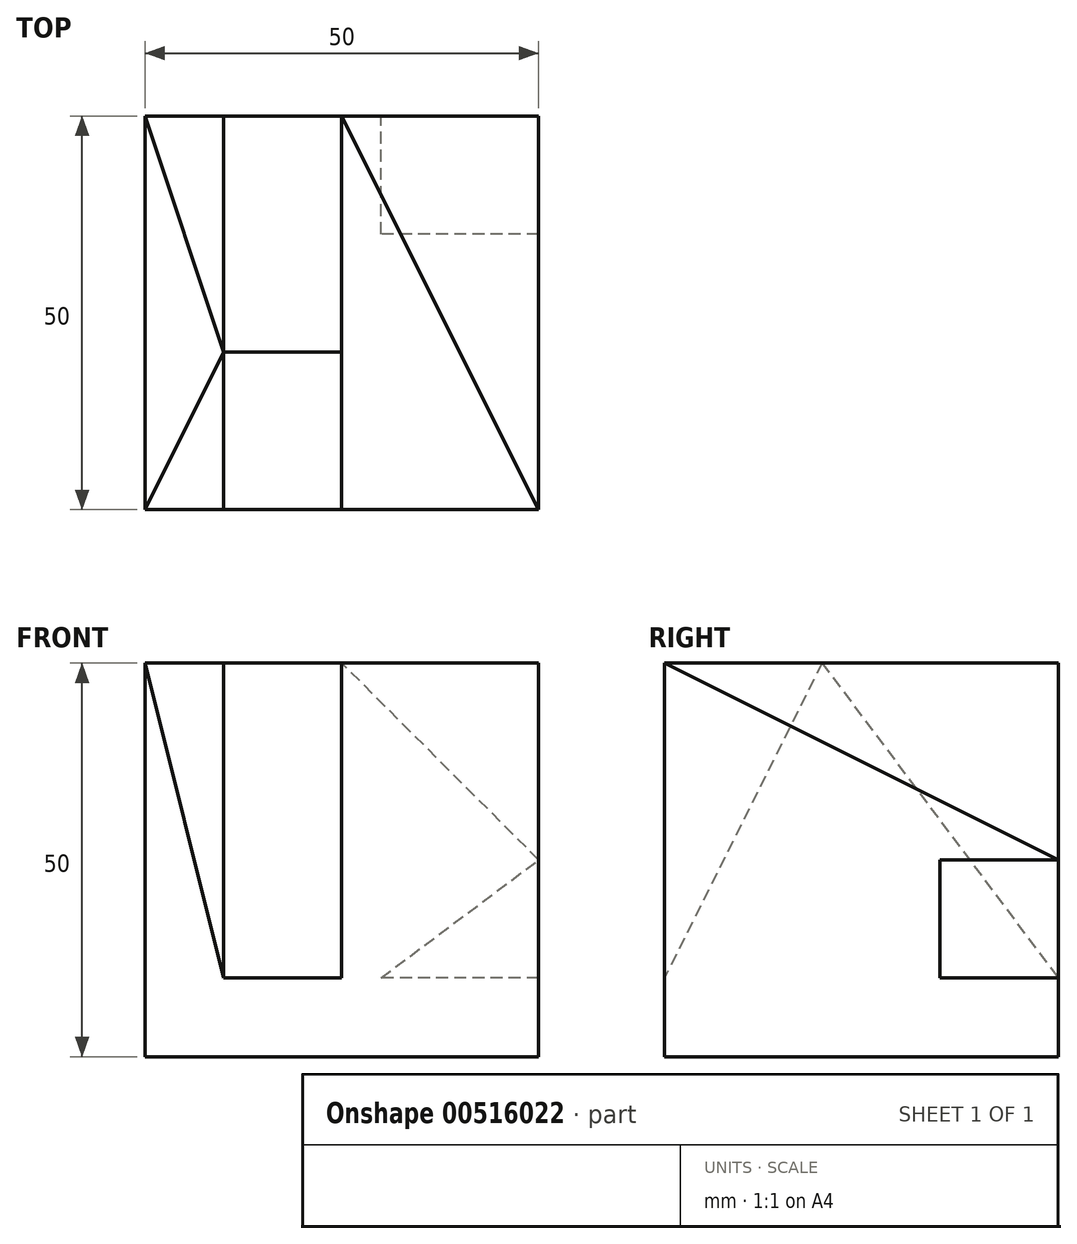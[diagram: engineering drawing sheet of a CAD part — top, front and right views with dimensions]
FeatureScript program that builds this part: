
annotation { "Feature Type Name" : "Feature", "Feature Type Description" : "" }
export const myFeature = defineFeature(function(context is Context, id is Id, definition is map)
    precondition{}
    {
        {
            var Q0;
            Q0=qCreatedBy(makeId("Top.planeOp"),FACE);
            var sketch = newSketch(context, id + "F0", { "sketchPlane" : qUnion([Q0])});
            skLineSegment(sketch, "E0.bottom", {"start": v(0, 0) * mm, "end": v(50, 0) * mm});
            skLineSegment(sketch, "E0.top", {"start": v(0, 50) * mm, "end": v(50, 50) * mm});
            skLineSegment(sketch, "E0.left", {"start": v(0, 0) * mm, "end": v(0, 50) * mm});
            skLineSegment(sketch, "E0.right", {"start": v(50, 0) * mm, "end": v(50, 50) * mm});
            skSolve(sketch);
        }
        {
            var Q0;
            Q0=makeQuery(id+"F0.imprint","IMPRINT",FACE,{"disambiguationData":[TD([[makeQuery(id+"F0.imprint","IMPRINT",EDGE,{"derivedFrom":sQuery(id+"F0.wireOp",EDGE,"E0.bottom")}),1.0]])]});
            extrude(context, id + "F1", {"entities" : qUnion([Q0]), "depth" : 50 * mm, "offsetDistance" : 25 * mm});
        }
        {
            var Q0;
            Q0=makeQuery(id+"F1.opExtrude","SWEPT_FACE",FACE,{"disambiguationData":[OSD([sQuery(id+"F0.wireOp",EDGE,"E0.top")])]});
            var sketch = newSketch(context, id + "F2", { "sketchPlane" : qUnion([Q0])});
            skLineSegment(sketch, "E1", {"start": v(-50, 10) * mm, "end": v(-30, 10) * mm});
            skLineSegment(sketch, "E2", {"start": v(-30, 10) * mm, "end": v(-50, 25) * mm});
            skLineSegment(sketch, "E3", {"start": v(-50, 25) * mm, "end": v(-50, 10) * mm});
            skSolve(sketch);
        }
        {
            var Q0;
            Q0=makeQuery(id+"F2.imprint","IMPRINT",FACE,{"disambiguationData":[TD([[makeQuery(id+"F2.imprint","IMPRINT",EDGE,{"derivedFrom":sQuery(id+"F2.wireOp",EDGE,"E1")}),1.0]])]});
            extrude(context, id + "F3", {"entities" : qUnion([Q0]), "operationType" : NewBodyOperationType.REMOVE, "oppositeDirection" : true, "depth" : 15 * mm, "offsetDistance" : 25 * mm});
        }
        {
            var Q0;
            Q0=makeQuery(id+"F1.opExtrude","CAP_FACE",FACE,{"disambiguationData":[OSD([sQuery(id+"F0.wireOp",EDGE,"E0.bottom"),sQuery(id+"F0.wireOp",EDGE,"E0.top"),sQuery(id+"F0.wireOp",EDGE,"E0.left"),sQuery(id+"F0.wireOp",EDGE,"E0.right")])],"isStart":false});
            var sketch = newSketch(context, id + "F4", { "sketchPlane" : qUnion([Q0])});
            skLineSegment(sketch, "E4.bottom", {"start": v(10, 0) * mm, "end": v(25, 0) * mm});
            skLineSegment(sketch, "E4.top", {"start": v(10, 20) * mm, "end": v(25, 20) * mm});
            skLineSegment(sketch, "E4.left", {"start": v(10, 0) * mm, "end": v(10, 20) * mm});
            skLineSegment(sketch, "E4.right", {"start": v(25, 0) * mm, "end": v(25, 20) * mm});
            skSolve(sketch);
        }
        {
            var Q0;
            Q0=makeQuery(id+"F1.opExtrude","SWEPT_FACE",FACE,{"disambiguationData":[OSD([sQuery(id+"F0.wireOp",EDGE,"E0.left")])]});
            var sketch = newSketch(context, id + "F5", { "sketchPlane" : qUnion([Q0])});
            skLineSegment(sketch, "E5", {"start": v(-20, 50) * mm, "end": v(0, 10) * mm});
            skSolve(sketch);
        }
        {
            var Q0;
            Q0=makeQuery(id+"F4.imprint","IMPRINT",FACE,{"disambiguationData":[TD([[makeQuery(id+"F4.imprint","IMPRINT",EDGE,{"derivedFrom":sQuery(id+"F4.wireOp",EDGE,"E4.bottom")}),1.0]])]});
            var Q1;
            Q1=sQuery(id+"F5.wireOp",EDGE,"E5");
            sweep(context, id + "F6", {"operationType" : NewBodyOperationType.REMOVE, "profiles" : qUnion([Q0]), "path" : qUnion([Q1])});
        }
        {
            var Q0;
            Q0=makeQuery(id+"F1.opExtrude","CAP_FACE",FACE,{"disambiguationData":[OSD([sQuery(id+"F0.wireOp",EDGE,"E0.bottom"),sQuery(id+"F0.wireOp",EDGE,"E0.top"),sQuery(id+"F0.wireOp",EDGE,"E0.left"),sQuery(id+"F0.wireOp",EDGE,"E0.right")])],"isStart":false});
            var sketch = newSketch(context, id + "F7", { "sketchPlane" : qUnion([Q0])});
            skLineSegment(sketch, "E6.bottom", {"start": v(10, 20) * mm, "end": v(25, 20) * mm});
            skLineSegment(sketch, "E6.top", {"start": v(10, 50) * mm, "end": v(25, 50) * mm});
            skLineSegment(sketch, "E6.left", {"start": v(10, 20) * mm, "end": v(10, 50) * mm});
            skLineSegment(sketch, "E6.right", {"start": v(25, 20) * mm, "end": v(25, 50) * mm});
            skSolve(sketch);
        }
        {
            var Q0;
            Q0=makeQuery(id+"F1.opExtrude","SWEPT_FACE",FACE,{"disambiguationData":[OSD([sQuery(id+"F0.wireOp",EDGE,"E0.left")])]});
            var sketch = newSketch(context, id + "F8", { "sketchPlane" : qUnion([Q0])});
            skLineSegment(sketch, "E7", {"start": v(-20, 50) * mm, "end": v(-50, 10) * mm});
            skSolve(sketch);
        }
        {
            var Q0;
            Q0=makeQuery(id+"F7.imprint","IMPRINT",FACE,{"disambiguationData":[TD([[makeQuery(id+"F7.imprint","IMPRINT",EDGE,{"derivedFrom":sQuery(id+"F7.wireOp",EDGE,"E6.bottom")}),1.0]])]});
            var Q1;
            Q1=sQuery(id+"F8.wireOp",EDGE,"E7");
            sweep(context, id + "F9", {"operationType" : NewBodyOperationType.REMOVE, "profiles" : qUnion([Q0]), "path" : qUnion([Q1])});
        }
        {
            var Q0;
            {var subQ0=sQuery(id+"F0.wireOp",EDGE,"E0.left");var subQ1=sQuery(id+"F0.wireOp",EDGE,"E0.top");var subQ4=sQuery(id+"F0.wireOp",EDGE,"E0.bottom");Q0=makeQuery(id+"F9.boolean.opBoolean","SPLIT",FACE,{"disambiguationData":[TD([makeQuery(id+"F1.opExtrude","SWEPT_FACE",FACE,{"disambiguationData":[OSD([subQ0])]})])],"derivedFrom":makeQuery(id+"F1.opExtrude","CAP_FACE",FACE,{"disambiguationData":[OSD([subQ4,subQ1,subQ0,sQuery(id+"F0.wireOp",EDGE,"E0.right")])],"isStart":false})});}
            var sketch = newSketch(context, id + "F10", { "sketchPlane" : qUnion([Q0])});
            skLineSegment(sketch, "E8", {"start": v(10, 20) * mm, "end": v(0, 0) * mm});
            skSolve(sketch);
        }
        {
            var Q0;
            Q0=makeQuery(id+"F1.opExtrude","SWEPT_FACE",FACE,{"disambiguationData":[OSD([sQuery(id+"F0.wireOp",EDGE,"E0.bottom")])]});
            var sketch = newSketch(context, id + "F11", { "sketchPlane" : qUnion([Q0])});
            skLineSegment(sketch, "E9", {"start": v(0, 50) * mm, "end": v(10, 10) * mm});
            skSolve(sketch);
        }
        {
            var Q0;
            Q0=makeQuery(id+"F6.boolean.opBoolean","COPY",FACE,{"derivedFrom":makeQuery(id+"F6.opSweep","SWEPT_FACE",FACE,{"disambiguationData":[OSD([sQuery(id+"F4.wireOp",EDGE,"E4.left"),sQuery(id+"F5.wireOp",EDGE,"E5")])]})});
            var Q1;
            Q1=sQuery(id+"F10.wireOp",EDGE,"E8");
            sweep(context, id + "F12", {"operationType" : NewBodyOperationType.REMOVE, "profiles" : qUnion([Q0]), "path" : qUnion([Q1])});
        }
        {
            var Q0;
            {var subQ0=sQuery(id+"F0.wireOp",EDGE,"E0.left");var subQ1=sQuery(id+"F0.wireOp",EDGE,"E0.top");var subQ4=sQuery(id+"F0.wireOp",EDGE,"E0.bottom");Q0=makeQuery(id+"F9.boolean.opBoolean","SPLIT",FACE,{"disambiguationData":[TD([makeQuery(id+"F1.opExtrude","SWEPT_FACE",FACE,{"disambiguationData":[OSD([subQ0])]})])],"derivedFrom":makeQuery(id+"F1.opExtrude","CAP_FACE",FACE,{"disambiguationData":[OSD([subQ4,subQ1,subQ0,sQuery(id+"F0.wireOp",EDGE,"E0.right")])],"isStart":false})});}
            var sketch = newSketch(context, id + "F13", { "sketchPlane" : qUnion([Q0])});
            skLineSegment(sketch, "E10", {"start": v(0, 50) * mm, "end": v(10, 20) * mm});
            skSolve(sketch);
        }
        {
            var Q0;
            Q0=makeQuery(id+"F1.opExtrude","SWEPT_FACE",FACE,{"disambiguationData":[OSD([sQuery(id+"F0.wireOp",EDGE,"E0.top")])]});
            var sketch = newSketch(context, id + "F14", { "sketchPlane" : qUnion([Q0])});
            skLineSegment(sketch, "E11", {"start": v(0, 50) * mm, "end": v(-10, 10) * mm});
            skSolve(sketch);
        }
        {
            var Q0;
            Q0=makeQuery(id+"F9.boolean.opBoolean","COPY",FACE,{"derivedFrom":makeQuery(id+"F9.opSweep","SWEPT_FACE",FACE,{"disambiguationData":[OSD([sQuery(id+"F7.wireOp",EDGE,"E6.left"),sQuery(id+"F8.wireOp",EDGE,"E7")])]})});
            var Q1;
            Q1=sQuery(id+"F13.wireOp",EDGE,"E10");
            sweep(context, id + "F15", {"operationType" : NewBodyOperationType.REMOVE, "profiles" : qUnion([Q0]), "path" : qUnion([Q1])});
        }
        {
            var Q0;
            {var subQ0=sQuery(id+"F0.wireOp",EDGE,"E0.top");var subQ3=sQuery(id+"F0.wireOp",EDGE,"E0.right");var subQ4=sQuery(id+"F0.wireOp",EDGE,"E0.bottom");Q0=makeQuery(id+"F9.boolean.opBoolean","SPLIT",FACE,{"disambiguationData":[TD([makeQuery(id+"F1.opExtrude","SWEPT_FACE",FACE,{"disambiguationData":[OSD([subQ3])]})])],"derivedFrom":makeQuery(id+"F1.opExtrude","CAP_FACE",FACE,{"disambiguationData":[OSD([subQ4,subQ0,sQuery(id+"F0.wireOp",EDGE,"E0.left"),subQ3])],"isStart":false})});}
            var sketch = newSketch(context, id + "F16", { "sketchPlane" : qUnion([Q0])});
            skLineSegment(sketch, "E12", {"start": v(25, 50) * mm, "end": v(50, 0) * mm});
            skSolve(sketch);
        }
        {
            var Q0;
            Q0=makeQuery(id+"F1.opExtrude","SWEPT_FACE",FACE,{"disambiguationData":[OSD([sQuery(id+"F0.wireOp",EDGE,"E0.right")])]});
            var sketch = newSketch(context, id + "F17", { "sketchPlane" : qUnion([Q0])});
            skLineSegment(sketch, "E13", {"start": v(0, 50) * mm, "end": v(50, 25) * mm});
            skSolve(sketch);
        }
        {
            var Q0;
            Q0=makeQuery(id+"F17.imprint","IMPRINT",FACE,{"disambiguationData":[TD([[makeQuery(id+"F17.imprint","IMPRINT",EDGE,{"derivedFrom":sQuery(id+"F17.wireOp",EDGE,"E13")}),1.0]])]});
            var Q1;
            Q1=sQuery(id+"F16.wireOp",EDGE,"E12");
            sweep(context, id + "F18", {"operationType" : NewBodyOperationType.REMOVE, "profiles" : qUnion([Q0]), "path" : qUnion([Q1])});
        }
    });
